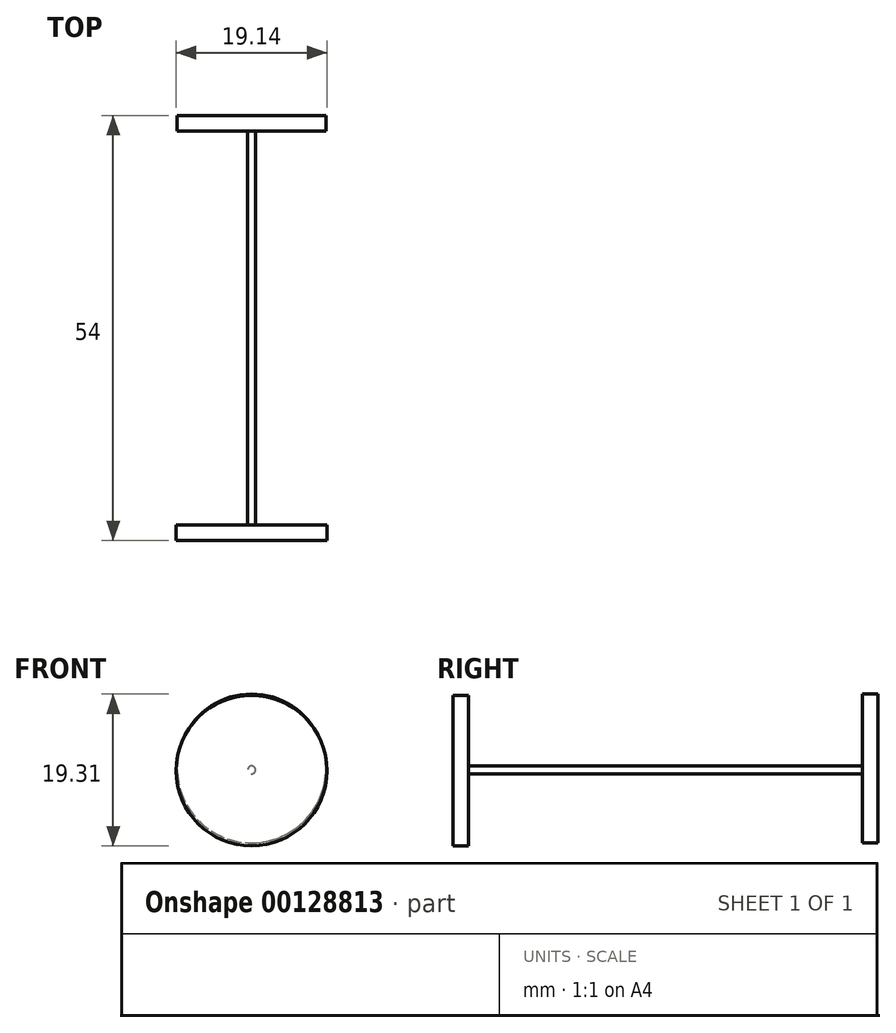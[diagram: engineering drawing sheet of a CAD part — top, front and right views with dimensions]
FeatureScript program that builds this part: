
annotation { "Feature Type Name" : "Feature", "Feature Type Description" : "" }
export const myFeature = defineFeature(function(context is Context, id is Id, definition is map)
    precondition{}
    {
        {
            var Q0;
            Q0=qCreatedBy(makeId("Front.planeOp"),FACE);
            var sketch = newSketch(context, id + "F0", { "sketchPlane" : qUnion([Q0])});
            skCircle(sketch, "E0", {"center": v(0, 8.7) * mm, "radius": 0.5 * mm});
            skSolve(sketch);
        }
        {
            var Q0;
            Q0 = qSketchRegion(id + "F0", true);
            extrude(context, id + "F1", {"entities" : qUnion([Q0]), "depth" : 50 * mm});
        }
        {
            var Q0;
            Q0=qCreatedBy(makeId("Front.planeOp"),FACE);
            cPlane(context, id + "F2", {"entities" : qUnion([Q0]), "cplaneType" : CPlaneType.OFFSET, "offset" : 42 * mm, "width" : 150 * mm, "height" : 150 * mm});
        }
        {
            var Q0;
            Q0=qCreatedBy(makeId("Front.planeOp"),FACE);
            var sketch = newSketch(context, id + "F3", { "sketchPlane" : qUnion([Q0])});
            skCircle(sketch, "E1", {"center": v(0, 8.9) * mm, "radius": 9.46 * mm});
            skSolve(sketch);
        }
        {
            var Q0;
            Q0 = qSketchRegion(id + "F3", true);
            extrude(context, id + "F4", {"entities" : qUnion([Q0]), "operationType" : NewBodyOperationType.ADD, "oppositeDirection" : true, "depth" : 2 * mm});
        }
        {
            var Q0;
            Q0=qCreatedBy(id+"F2.planeOp",FACE);
            cPlane(context, id + "F5", {"entities" : qUnion([Q0]), "cplaneType" : CPlaneType.OFFSET, "offset" : 8 * mm, "width" : 150 * mm, "height" : 150 * mm});
        }
        {
            var Q0;
            Q0=qCreatedBy(id+"F5.planeOp",FACE);
            var sketch = newSketch(context, id + "F6", { "sketchPlane" : qUnion([Q0])});
            skCircle(sketch, "E2", {"center": v(0, 8.63) * mm, "radius": 9.57 * mm});
            skSolve(sketch);
        }
        {
            var Q0;
            Q0 = qSketchRegion(id + "F6", true);
            extrude(context, id + "F7", {"entities" : qUnion([Q0]), "operationType" : NewBodyOperationType.ADD, "depth" : 2 * mm});
        }
    });
